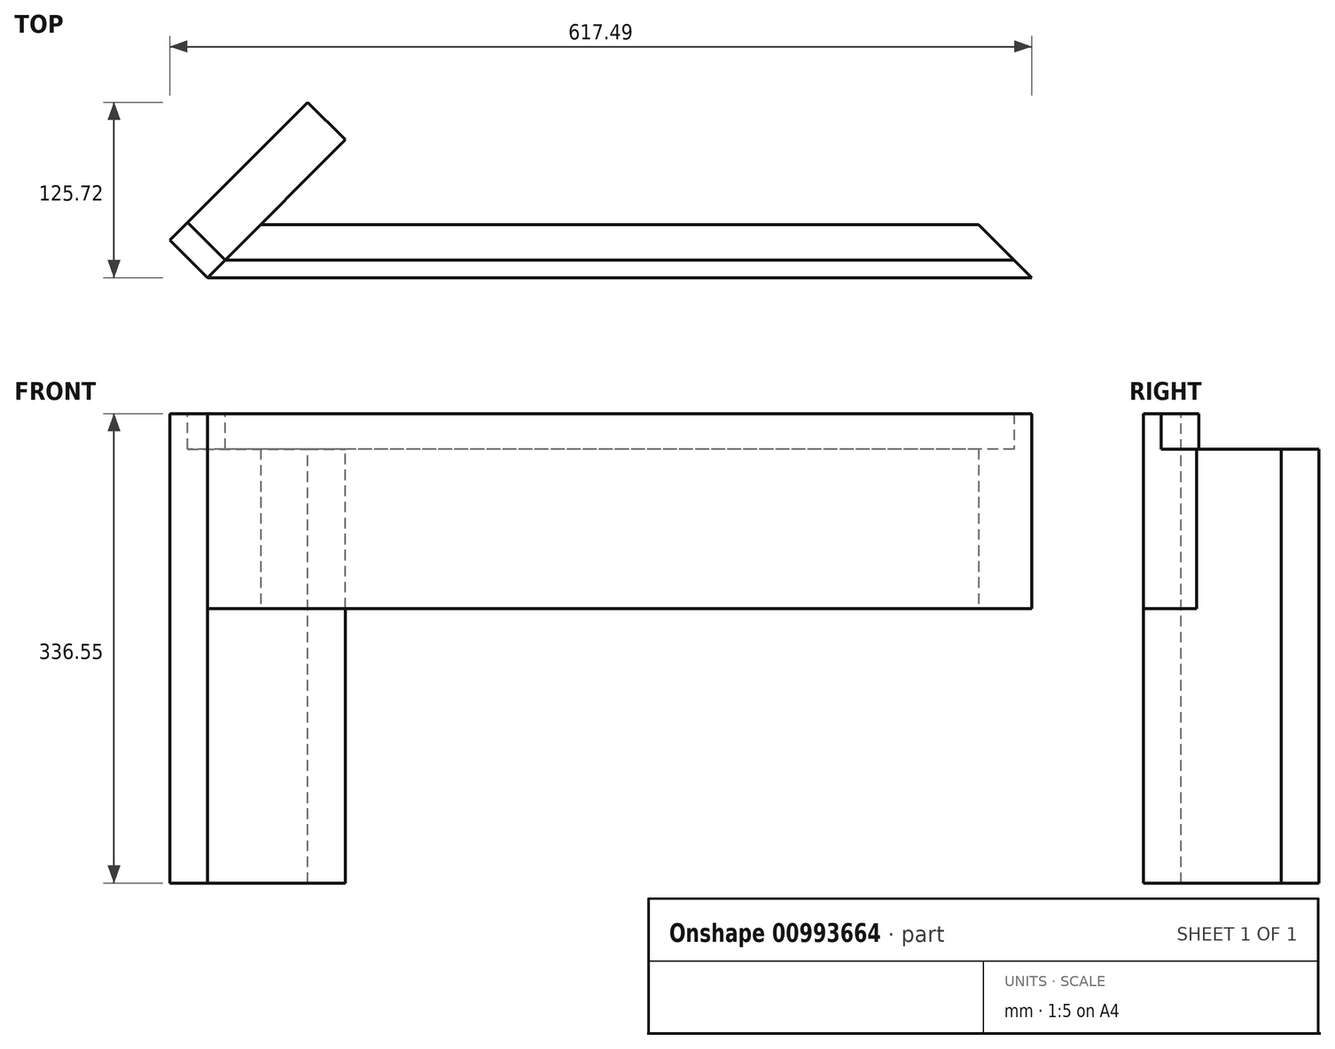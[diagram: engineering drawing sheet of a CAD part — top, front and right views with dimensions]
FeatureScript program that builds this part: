
annotation { "Feature Type Name" : "Feature", "Feature Type Description" : "" }
export const myFeature = defineFeature(function(context is Context, id is Id, definition is map)
    precondition{}
    {
        {
            var Q0;
            Q0=qCreatedBy(makeId("Top.planeOp"),FACE);
            var sketch = newSketch(context, id + "F0", { "sketchPlane" : qUnion([Q0])});
            skLineSegment(sketch, "E0", {"start": v(0, 0) * mm, "end": v(590.55, 0) * mm});
            skLineSegment(sketch, "E1", {"start": v(590.55, 0) * mm, "end": v(552.45, 38.1) * mm});
            skLineSegment(sketch, "E2", {"start": v(552.45, 38.1) * mm, "end": v(38.1, 38.1) * mm});
            skLineSegment(sketch, "E3", {"start": v(38.1, 38.1) * mm, "end": v(0, 0) * mm});
            skSolve(sketch);
        }
        {
            var Q0;
            Q0 = qSketchRegion(id + "F0", true);
            extrude(context, id + "F1", {"entities" : qUnion([Q0]), "depth" : 139.7 * mm, "offsetDistance" : 25.4 * mm});
        }
        {
            var Q0;
            Q0=makeQuery(id+"F1.opExtrude","CAP_FACE",FACE,{"disambiguationData":[OSD([sQuery(id+"F0.wireOp",EDGE,"E0"),sQuery(id+"F0.wireOp",EDGE,"E1"),sQuery(id+"F0.wireOp",EDGE,"E2"),sQuery(id+"F0.wireOp",EDGE,"E3")])],"isStart":false});
            var sketch = newSketch(context, id + "F2", { "sketchPlane" : qUnion([Q0])});
            skLineSegment(sketch, "E4.bottom", {"start": v(590.55, 12.7) * mm, "end": v(0, 12.7) * mm});
            skLineSegment(sketch, "E4.top", {"start": v(590.55, 38.1) * mm, "end": v(0, 38.1) * mm});
            skLineSegment(sketch, "E4.left", {"start": v(590.55, 12.7) * mm, "end": v(590.55, 38.1) * mm});
            skLineSegment(sketch, "E4.right", {"start": v(0, 12.7) * mm, "end": v(0, 38.1) * mm});
            skSolve(sketch);
        }
        {
            var Q0;
            Q0 = qSketchRegion(id + "F2", true);
            extrude(context, id + "F3", {"entities" : qUnion([Q0]), "operationType" : NewBodyOperationType.REMOVE, "oppositeDirection" : true, "depth" : 25.4 * mm, "offsetDistance" : 25.4 * mm});
        }
        {
            var Q0;
            Q0=makeQuery(id+"F1.opExtrude","CAP_FACE",FACE,{"disambiguationData":[OSD([sQuery(id+"F0.wireOp",EDGE,"E0"),sQuery(id+"F0.wireOp",EDGE,"E1"),sQuery(id+"F0.wireOp",EDGE,"E2"),sQuery(id+"F0.wireOp",EDGE,"E3")])],"isStart":false});
            var sketch = newSketch(context, id + "F4", { "sketchPlane" : qUnion([Q0])});
            skLineSegment(sketch, "E5", {"start": v(0, 0) * mm, "end": v(-26.94, 26.94) * mm});
            skLineSegment(sketch, "E6", {"start": v(-26.94, 26.94) * mm, "end": v(71.84, 125.72) * mm});
            skLineSegment(sketch, "E7", {"start": v(0, 0) * mm, "end": v(98.78, 98.78) * mm});
            skLineSegment(sketch, "E8", {"start": v(71.84, 125.72) * mm, "end": v(98.78, 98.78) * mm});
            skSolve(sketch);
        }
        {
            var Q0;
            Q0 = qSketchRegion(id + "F4", true);
            extrude(context, id + "F5", {"entities" : qUnion([Q0]), "oppositeDirection" : true, "depth" : 336.55 * mm, "offsetDistance" : 25.4 * mm});
        }
        {
            var Q0;
            Q0=makeQuery(id+"F5.opExtrude","CAP_FACE",FACE,{"disambiguationData":[OSD([sQuery(id+"F4.wireOp",EDGE,"E5"),sQuery(id+"F4.wireOp",EDGE,"E6"),sQuery(id+"F4.wireOp",EDGE,"E7"),sQuery(id+"F4.wireOp",EDGE,"E8")])],"isStart":true});
            var sketch = newSketch(context, id + "F6", { "sketchPlane" : qUnion([Q0])});
            skLineSegment(sketch, "E9", {"start": v(71.84, 125.72) * mm, "end": v(98.78, 98.78) * mm});
            skLineSegment(sketch, "E10", {"start": v(98.78, 98.78) * mm, "end": v(12.7, 12.7) * mm});
            skLineSegment(sketch, "E11", {"start": v(12.7, 12.7) * mm, "end": v(-14.24, 39.64) * mm});
            skLineSegment(sketch, "E12", {"start": v(-14.24, 39.64) * mm, "end": v(71.84, 125.72) * mm});
            skSolve(sketch);
        }
        {
            var Q0;
            Q0 = qSketchRegion(id + "F6", true);
            extrude(context, id + "F7", {"entities" : qUnion([Q0]), "operationType" : NewBodyOperationType.REMOVE, "oppositeDirection" : true, "depth" : 25.4 * mm, "offsetDistance" : 25.4 * mm});
        }
    });
